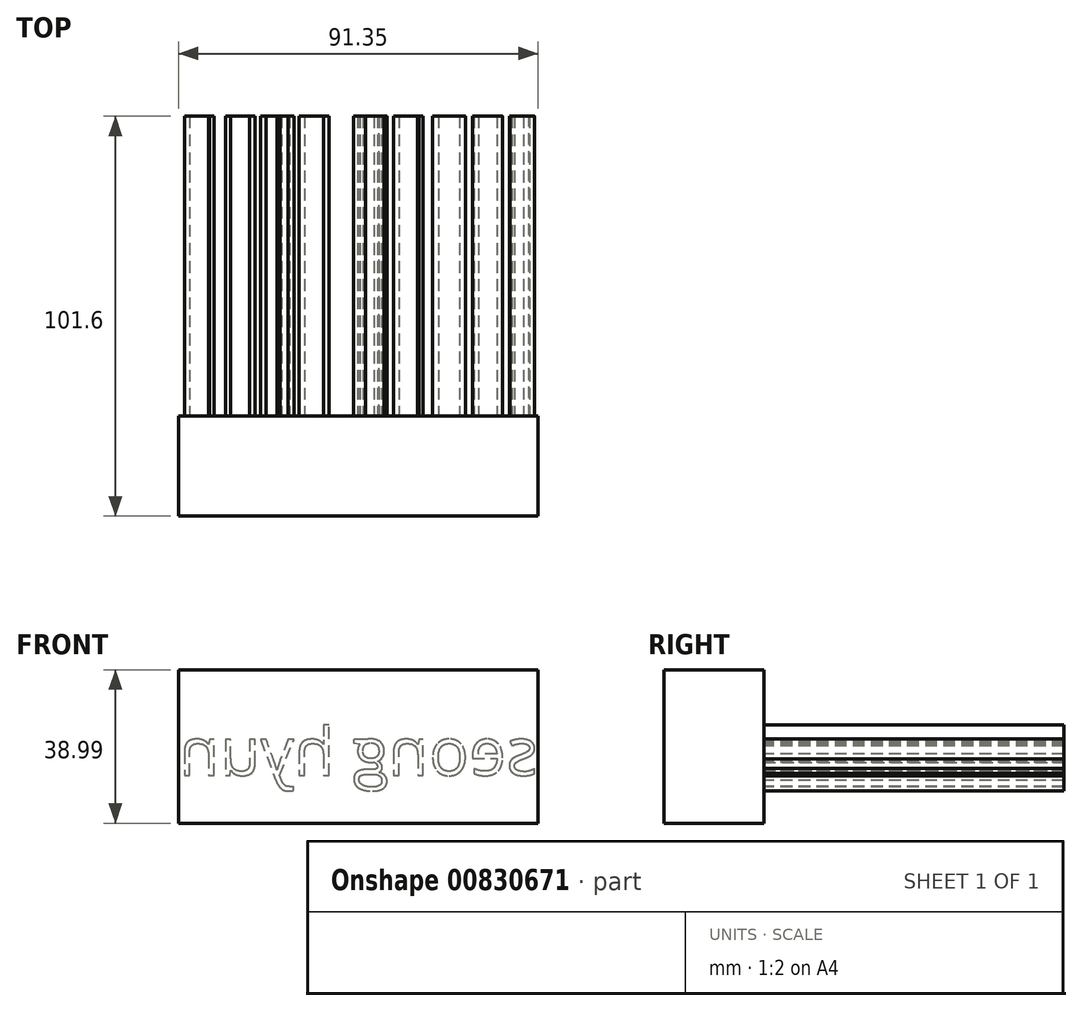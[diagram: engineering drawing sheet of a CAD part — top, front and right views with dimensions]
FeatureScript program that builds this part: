
annotation { "Feature Type Name" : "Feature", "Feature Type Description" : "" }
export const myFeature = defineFeature(function(context is Context, id is Id, definition is map)
    precondition{}
    {
        {
            var Q0;
            Q0=qCreatedBy(makeId("Front.planeOp"),FACE);
            var sketch = newSketch(context, id + "F0", { "sketchPlane" : qUnion([Q0])});
            skLineSegment(sketch, "E0.bottom", {"start": v(0, 0) * mm, "end": v(91.35, 0) * mm});
            skLineSegment(sketch, "E0.top", {"start": v(0, 39) * mm, "end": v(91.35, 39) * mm});
            skLineSegment(sketch, "E0.left", {"start": v(0, 0) * mm, "end": v(0, 39) * mm});
            skLineSegment(sketch, "E0.right", {"start": v(91.35, 0) * mm, "end": v(91.35, 39) * mm});
            skSolve(sketch);
        }
        {
            var Q0;
            Q0=makeQuery(id+"F0.imprint","IMPRINT",FACE,{"disambiguationData":[TD([[makeQuery(id+"F0.imprint","IMPRINT",EDGE,{"derivedFrom":sQuery(id+"F0.wireOp",EDGE,"E0.bottom")}),1.0]])]});
            extrude(context, id + "F1", {"entities" : qUnion([Q0]), "depth" : 25.4 * mm, "offsetDistance" : 25.4 * mm});
        }
        {
            var Q0;
            Q0=makeQuery(id+"F1.opExtrude","CAP_FACE",FACE,{"disambiguationData":[OSD([sQuery(id+"F0.wireOp",EDGE,"E0.bottom"),sQuery(id+"F0.wireOp",EDGE,"E0.top"),sQuery(id+"F0.wireOp",EDGE,"E0.left"),sQuery(id+"F0.wireOp",EDGE,"E0.right")])],"isStart":true});
            var sketch = newSketch(context, id + "F2", { "sketchPlane" : qUnion([Q0])});
            skText(sketch, "E1", { "text": "seong hyun", "fontName": "OpenSans-Regular.ttf"});
            const initialGuessF2  = {"E1": [-0.09135, 0.0122, 1, 0, 0.01214]};
            skSetInitialGuess(sketch, initialGuessF2);
            skSolve(sketch);
        }
        {
            var Q0;
            Q0 = qSketchRegion(id + "F2", true);
            extrude(context, id + "F3", {"entities" : qUnion([Q0]), "operationType" : NewBodyOperationType.ADD, "depth" : 76.2 * mm, "offsetDistance" : 25.4 * mm});
        }
    });
